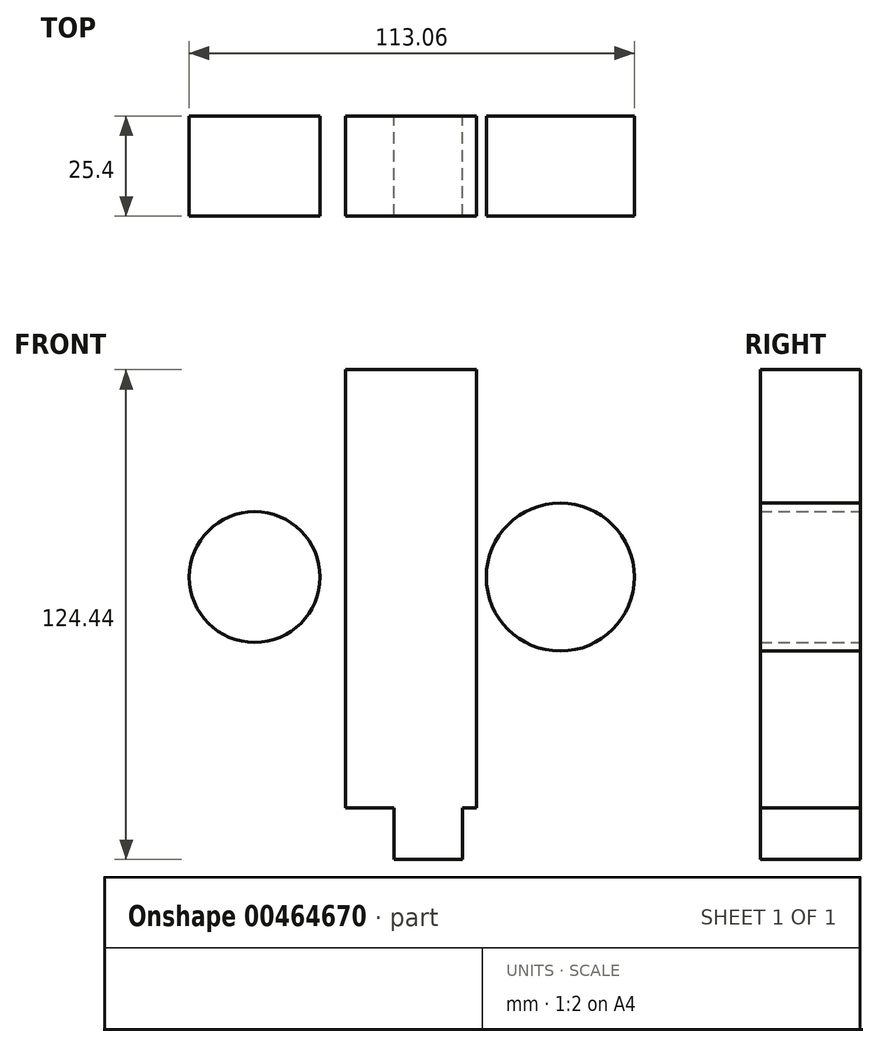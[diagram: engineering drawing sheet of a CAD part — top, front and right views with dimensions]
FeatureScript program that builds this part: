
annotation { "Feature Type Name" : "Feature", "Feature Type Description" : "" }
export const myFeature = defineFeature(function(context is Context, id is Id, definition is map)
    precondition{}
    {
        {
            var Q0;
            Q0=qCreatedBy(makeId("Front.planeOp"),FACE);
            var sketch = newSketch(context, id + "F0", { "sketchPlane" : qUnion([Q0])});
            skLineSegment(sketch, "E0.bottom", {"start": v(-12.3, 52.7) * mm, "end": v(21.02, 52.7) * mm});
            skLineSegment(sketch, "E0.top", {"start": v(-12.3, -58.61) * mm, "end": v(21.02, -58.61) * mm});
            skLineSegment(sketch, "E0.left", {"start": v(-12.3, 52.7) * mm, "end": v(-12.3, -58.61) * mm});
            skLineSegment(sketch, "E0.right", {"start": v(21.02, 52.7) * mm, "end": v(21.02, -58.61) * mm});
            skSolve(sketch);
        }
        {
            var Q0;
            Q0 = qSketchRegion(id + "F0", true);
            extrude(context, id + "F1", {"entities" : qUnion([Q0]), "depth" : 25.4 * mm});
        }
        {
            var Q0;
            Q0=qCreatedBy(makeId("Front.planeOp"),FACE);
            var sketch = newSketch(context, id + "F2", { "sketchPlane" : qUnion([Q0])});
            skCircle(sketch, "E1", {"center": v(-35.35, 0) * mm, "radius": 16.62 * mm});
            skCircle(sketch, "E2", {"center": v(42.3, 0) * mm, "radius": 18.8 * mm});
            skSolve(sketch);
        }
        {
            var Q0;
            Q0 = qSketchRegion(id + "F2", true);
            extrude(context, id + "F3", {"entities" : qUnion([Q0]), "depth" : 25.4 * mm});
        }
        {
            var Q0;
            Q0=qCreatedBy(makeId("Front.planeOp"),FACE);
            var sketch = newSketch(context, id + "F4", { "sketchPlane" : qUnion([Q0])});
            skArc(sketch, "E3", {"start": v(0, 74.69) * mm, "mid": v(-36.22, 57.71) * mm, "end": v(-40.67, 17.96) * mm});
            skArc(sketch, "E4", {"start": v(52.22, 17.96) * mm, "mid": v(41.28, 60.3) * mm, "end": v(0, 74.69) * mm});
            skLineSegment(sketch, "E5.bottom", {"start": v(0, -2.6) * mm, "end": v(17.48, -2.6) * mm});
            skLineSegment(sketch, "E5.top", {"start": v(0, -71.73) * mm, "end": v(17.48, -71.73) * mm});
            skLineSegment(sketch, "E5.left", {"start": v(0, -2.6) * mm, "end": v(0, -71.73) * mm});
            skLineSegment(sketch, "E5.right", {"start": v(17.48, -2.6) * mm, "end": v(17.48, -71.73) * mm});
            skLineSegment(sketch, "E6.bottom", {"start": v(0, -57.55) * mm, "end": v(-6.63, -57.55) * mm});
            skLineSegment(sketch, "E6.top", {"start": v(0, -56.84) * mm, "end": v(-6.63, -56.84) * mm});
            skLineSegment(sketch, "E6.left", {"start": v(0, -57.55) * mm, "end": v(0, -56.84) * mm});
            skLineSegment(sketch, "E6.right", {"start": v(-6.63, -57.55) * mm, "end": v(-6.63, -56.84) * mm});
            skSolve(sketch);
        }
        {
            var Q0;
            Q0 = qSketchRegion(id + "F4", true);
            extrude(context, id + "F5", {"entities" : qUnion([Q0]), "operationType" : NewBodyOperationType.ADD, "depth" : 25.4 * mm});
        }
    });
